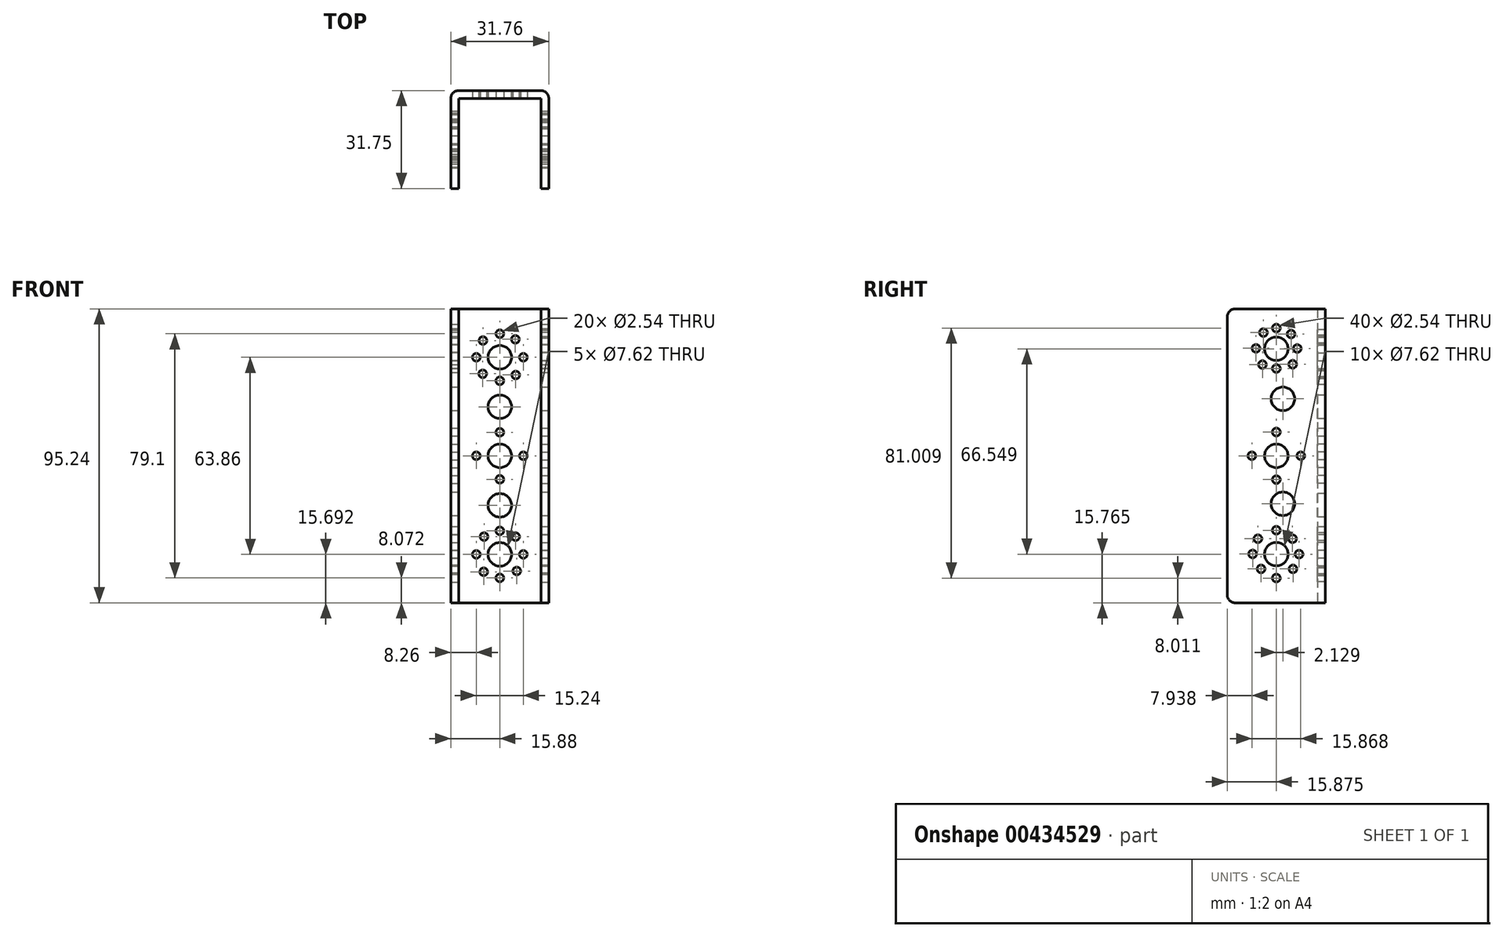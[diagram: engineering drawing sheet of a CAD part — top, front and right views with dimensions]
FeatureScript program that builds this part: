
annotation { "Feature Type Name" : "Feature", "Feature Type Description" : "" }
export const myFeature = defineFeature(function(context is Context, id is Id, definition is map)
    precondition{}
    {
        {
            var Q0;
            Q0=qCreatedBy(makeId("Front.planeOp"),FACE);
            var sketch = newSketch(context, id + "F0", { "sketchPlane" : qUnion([Q0])});
            skLineSegment(sketch, "E0.bottom", {"start": v(-15.87, 47.63) * mm, "end": v(15.88, 47.63) * mm});
            skLineSegment(sketch, "E0.top", {"start": v(-15.88, -47.62) * mm, "end": v(15.88, -47.62) * mm});
            skLineSegment(sketch, "E0.left", {"start": v(-15.87, 47.63) * mm, "end": v(-15.88, -47.62) * mm});
            skLineSegment(sketch, "E0.right", {"start": v(15.88, 47.63) * mm, "end": v(15.88, -47.62) * mm});
            skPoint(sketch, "E0.middle", {"position": v(0, 0) * mm});
            skSolve(sketch);
        }
        {
            var Q0;
            Q0=makeQuery(id+"F0.imprint","IMPRINT",FACE,{"disambiguationData":[TD([[makeQuery(id+"F0.imprint","IMPRINT",EDGE,{"derivedFrom":sQuery(id+"F0.wireOp",EDGE,"E0.bottom")}),-1.0]])]});
            extrude(context, id + "F1", {"entities" : qUnion([Q0]), "flatOperationType" : FlatOperationType.REMOVE, "offsetDistance" : 25.4 * mm, "depth" : 31.75 * mm, "domain" : OperationDomain.MODEL});
        }
        {
            var Q0;
            Q0=makeQuery(id+"F1.opExtrude","CAP_FACE",FACE,{"disambiguationData":[OSD([sQuery(id+"F0.wireOp",EDGE,"E0.bottom"),sQuery(id+"F0.wireOp",EDGE,"E0.top"),sQuery(id+"F0.wireOp",EDGE,"E0.left"),sQuery(id+"F0.wireOp",EDGE,"E0.right")])],"isStart":false});
            var Q1;
            Q1=makeQuery(id+"F1.opExtrude","SWEPT_FACE",FACE,{"disambiguationData":[OSD([sQuery(id+"F0.wireOp",EDGE,"E0.bottom")])]});
            var Q2;
            Q2=makeQuery(id+"F1.opExtrude","SWEPT_FACE",FACE,{"disambiguationData":[OSD([sQuery(id+"F0.wireOp",EDGE,"E0.top")])]});
            shell(context, id + "F2", {"entities" : qUnion([Q0, Q1, Q2]), "thickness" : 2.54 * mm});
        }
        {
            var Q0;
            {var subQ0=sQuery(id+"F0.wireOp",EDGE,"E0.right");var subQ1=sQuery(id+"F0.wireOp",EDGE,"E0.left");var subQ2=sQuery(id+"F0.wireOp",EDGE,"E0.top");var subQ3=sQuery(id+"F0.wireOp",EDGE,"E0.bottom");Q0=makeQuery(id+"F2.opShell","OFFSET_FACE",FACE,{"disambiguationData":[OSD([subQ3,subQ2,subQ1,subQ0]),TDD([makeQuery(id+"F1.opExtrude","CAP_FACE",FACE,{"disambiguationData":[OSD([subQ3,subQ2,subQ1,subQ0])],"isStart":true})])]});}
            var sketch = newSketch(context, id + "F3", { "sketchPlane" : qUnion([Q0])});
            skCircle(sketch, "E1", {"center": v(0, 0) * mm, "radius": 3.81 * mm});
            skPoint(sketch, "E2.centerSnap0", {"position": v(-13.33, 0) * mm});
            skSolve(sketch);
        }
        {
            var Q0;
            Q0=sQuery(id+"F3.wireOp",VERTEX,"E1.center");
            var Q1;
            Q1=makeQuery(id+"F1.opExtrude","SWEPT_BODY",BODY,{"disambiguationData":[OSD([sQuery(id+"F0.wireOp",EDGE,"E0.bottom"),sQuery(id+"F0.wireOp",EDGE,"E0.top"),sQuery(id+"F0.wireOp",EDGE,"E0.left"),sQuery(id+"F0.wireOp",EDGE,"E0.right")])]});
            hole(context, id + "F4", {"style" : HoleStyle.SIMPLE, "endStyle" : HoleEndStyle.THROUGH, "holeDiameter" : 7.62 * mm, "tappedDepth" : 12.7 * mm, "tapClearance" : 3, "locations" : qUnion([Q0]), "scope" : qUnion([Q1])});
        }
        {
            var Q0;
            Q0=makeQuery(id+"F1.opExtrude","CAP_EDGE",EDGE,{"disambiguationData":[OSD([sQuery(id+"F0.wireOp",EDGE,"E0.right")])],"isStart":true});
            var Q1;
            Q1=makeQuery(id+"F1.opExtrude","CAP_EDGE",EDGE,{"disambiguationData":[OSD([sQuery(id+"F0.wireOp",EDGE,"E0.left")])],"isStart":true});
            var Q2;
            Q2=makeQuery(id+"F1.opExtrude","CAP_EDGE",EDGE,{"disambiguationData":[OSD([sQuery(id+"F0.wireOp",EDGE,"E0.bottom")])],"isStart":false});
            var Q3;
            {var subQ0=sQuery(id+"F0.wireOp",EDGE,"E0.bottom");Q3=makeQuery(id+"F2.opShell","OFFSET_EDGE",EDGE,{"disambiguationData":[OSD([subQ0]),TDD([makeQuery(id+"F1.opExtrude","CAP_EDGE",EDGE,{"disambiguationData":[OSD([subQ0])],"isStart":false})])]});}
            var Q4;
            Q4=makeQuery(id+"F1.opExtrude","CAP_EDGE",EDGE,{"disambiguationData":[OSD([sQuery(id+"F0.wireOp",EDGE,"E0.top")])],"isStart":false});
            var Q5;
            {var subQ0=sQuery(id+"F0.wireOp",EDGE,"E0.top");Q5=makeQuery(id+"F2.opShell","OFFSET_EDGE",EDGE,{"disambiguationData":[OSD([subQ0]),TDD([makeQuery(id+"F1.opExtrude","CAP_EDGE",EDGE,{"disambiguationData":[OSD([subQ0])],"isStart":false})])]});}
            fillet(context, id + "F5", {"entities" : qUnion([Q0, Q1, Q2, Q3, Q4, Q5]), "radius" : 2.54 * mm, "tangentPropagation" : true, "allowEdgeOverflow" : false});
        }
        {
            var Q0;
            {var subQ0=sQuery(id+"F0.wireOp",EDGE,"E0.right");var subQ1=sQuery(id+"F0.wireOp",EDGE,"E0.left");var subQ2=sQuery(id+"F0.wireOp",EDGE,"E0.top");var subQ3=sQuery(id+"F0.wireOp",EDGE,"E0.bottom");Q0=makeQuery(id+"F2.opShell","OFFSET_FACE",FACE,{"disambiguationData":[OSD([subQ3,subQ2,subQ1,subQ0]),TDD([makeQuery(id+"F1.opExtrude","CAP_FACE",FACE,{"disambiguationData":[OSD([subQ3,subQ2,subQ1,subQ0])],"isStart":true})])]});}
            var sketch = newSketch(context, id + "F6", { "sketchPlane" : qUnion([Q0])});
            skCircle(sketch, "E3", {"center": v(0, 7.62) * mm, "radius": 1.27 * mm});
            skCircle(sketch, "E4", {"center": v(7.62, 0) * mm, "radius": 1.27 * mm});
            skCircle(sketch, "E5", {"center": v(-7.62, 0) * mm, "radius": 1.27 * mm});
            skCircle(sketch, "E6", {"center": v(0, -7.62) * mm, "radius": 1.27 * mm});
            skSolve(sketch);
        }
        {
            var Q0;
            Q0=sQuery(id+"F6.wireOp",VERTEX,"E3.center");
            var Q1;
            Q1=sQuery(id+"F6.wireOp",VERTEX,"E4.center");
            var Q2;
            Q2=sQuery(id+"F6.wireOp",VERTEX,"E6.center");
            var Q3;
            Q3=sQuery(id+"F6.wireOp",VERTEX,"E5.center");
            var Q4;
            Q4=makeQuery(id+"F1.opExtrude","SWEPT_BODY",BODY,{"disambiguationData":[OSD([sQuery(id+"F0.wireOp",EDGE,"E0.bottom"),sQuery(id+"F0.wireOp",EDGE,"E0.top"),sQuery(id+"F0.wireOp",EDGE,"E0.left"),sQuery(id+"F0.wireOp",EDGE,"E0.right")])]});
            hole(context, id + "F7", {"style" : HoleStyle.SIMPLE, "endStyle" : HoleEndStyle.THROUGH, "holeDiameter" : 2.54 * mm, "tappedDepth" : 12.7 * mm, "tapClearance" : 3, "locations" : qUnion([Q0, Q1, Q2, Q3]), "scope" : qUnion([Q4])});
        }
        {
            var Q0;
            {var subQ0=sQuery(id+"F0.wireOp",EDGE,"E0.right");var subQ1=sQuery(id+"F0.wireOp",EDGE,"E0.left");var subQ2=sQuery(id+"F0.wireOp",EDGE,"E0.top");var subQ3=sQuery(id+"F0.wireOp",EDGE,"E0.bottom");Q0=makeQuery(id+"F2.opShell","OFFSET_FACE",FACE,{"disambiguationData":[OSD([subQ3,subQ2,subQ1,subQ0]),TDD([makeQuery(id+"F1.opExtrude","CAP_FACE",FACE,{"disambiguationData":[OSD([subQ3,subQ2,subQ1,subQ0])],"isStart":true})])]});}
            var sketch = newSketch(context, id + "F8", { "sketchPlane" : qUnion([Q0])});
            skCircle(sketch, "E7", {"center": v(0, 31.93) * mm, "radius": 3.81 * mm});
            skCircle(sketch, "E8", {"center": v(0, -31.93) * mm, "radius": 3.81 * mm});
            skSolve(sketch);
        }
        {
            var Q0;
            Q0=sQuery(id+"F8.wireOp",VERTEX,"E7.center");
            var Q1;
            Q1=sQuery(id+"F8.wireOp",VERTEX,"E8.center");
            var Q2;
            Q2=makeQuery(id+"F1.opExtrude","SWEPT_BODY",BODY,{"disambiguationData":[OSD([sQuery(id+"F0.wireOp",EDGE,"E0.bottom"),sQuery(id+"F0.wireOp",EDGE,"E0.top"),sQuery(id+"F0.wireOp",EDGE,"E0.left"),sQuery(id+"F0.wireOp",EDGE,"E0.right")])]});
            hole(context, id + "F9", {"style" : HoleStyle.SIMPLE, "endStyle" : HoleEndStyle.THROUGH, "holeDiameter" : 7.62 * mm, "tappedDepth" : 12.7 * mm, "tapClearance" : 3, "locations" : qUnion([Q0, Q1]), "scope" : qUnion([Q2])});
        }
        {
            var Q0;
            {var subQ0=sQuery(id+"F0.wireOp",EDGE,"E0.right");var subQ1=sQuery(id+"F0.wireOp",EDGE,"E0.left");var subQ2=sQuery(id+"F0.wireOp",EDGE,"E0.top");var subQ3=sQuery(id+"F0.wireOp",EDGE,"E0.bottom");Q0=makeQuery(id+"F2.opShell","OFFSET_FACE",FACE,{"disambiguationData":[OSD([subQ3,subQ2,subQ1,subQ0]),TDD([makeQuery(id+"F1.opExtrude","CAP_FACE",FACE,{"disambiguationData":[OSD([subQ3,subQ2,subQ1,subQ0])],"isStart":true})])]});}
            var sketch = newSketch(context, id + "F10", { "sketchPlane" : qUnion([Q0])});
            skCircle(sketch, "E9", {"center": v(0, 39.55) * mm, "radius": 1.27 * mm});
            skCircle(sketch, "E10", {"center": v(7.62, 31.93) * mm, "radius": 1.27 * mm});
            skCircle(sketch, "E11", {"center": v(0, 24.31) * mm, "radius": 1.27 * mm});
            skCircle(sketch, "E12", {"center": v(-7.62, 31.93) * mm, "radius": 1.27 * mm});
            skPoint(sketch, "E13.start.orphan", {"position": v(0, 31.93) * mm});
            skCircle(sketch, "E14", {"center": v(-5.47, 37.35) * mm, "radius": 1.27 * mm});
            skCircle(sketch, "E15", {"center": v(5.04, 37.77) * mm, "radius": 1.27 * mm});
            skCircle(sketch, "E16", {"center": v(5.14, 26.2) * mm, "radius": 1.27 * mm});
            skCircle(sketch, "E17", {"center": v(-5.54, 26.6) * mm, "radius": 1.27 * mm});
            skCircle(sketch, "E18", {"center": v(0, -24.3) * mm, "radius": 1.27 * mm});
            skCircle(sketch, "E19", {"center": v(7.62, -31.93) * mm, "radius": 1.27 * mm});
            skCircle(sketch, "E20", {"center": v(0, -39.55) * mm, "radius": 1.27 * mm});
            skCircle(sketch, "E21", {"center": v(-7.62, -31.93) * mm, "radius": 1.27 * mm});
            skPoint(sketch, "E22.orphan", {"position": v(0, -31.93) * mm});
            skCircle(sketch, "E23", {"center": v(5.12, -26.18) * mm, "radius": 1.27 * mm});
            skCircle(sketch, "E24", {"center": v(-5.11, -26.17) * mm, "radius": 1.27 * mm});
            skCircle(sketch, "E25", {"center": v(5.5, -37.31) * mm, "radius": 1.27 * mm});
            skCircle(sketch, "E26", {"center": v(-5.21, -37.6) * mm, "radius": 1.27 * mm});
            skSolve(sketch);
        }
        {
            var Q0;
            Q0=sQuery(id+"F10.wireOp",VERTEX,"E14.center");
            var Q1;
            Q1=sQuery(id+"F10.wireOp",VERTEX,"E9.center");
            var Q2;
            Q2=sQuery(id+"F10.wireOp",VERTEX,"E15.center");
            var Q3;
            Q3=sQuery(id+"F10.wireOp",VERTEX,"E10.center");
            var Q4;
            Q4=sQuery(id+"F10.wireOp",VERTEX,"E16.center");
            var Q5;
            Q5=sQuery(id+"F10.wireOp",VERTEX,"E11.center");
            var Q6;
            Q6=sQuery(id+"F10.wireOp",VERTEX,"E17.center");
            var Q7;
            Q7=sQuery(id+"F10.wireOp",VERTEX,"E12.center");
            var Q8;
            Q8=sQuery(id+"F10.wireOp",VERTEX,"E18.center");
            var Q9;
            Q9=sQuery(id+"F10.wireOp",VERTEX,"E23.center");
            var Q10;
            Q10=sQuery(id+"F10.wireOp",VERTEX,"E19.center");
            var Q11;
            Q11=sQuery(id+"F10.wireOp",VERTEX,"E25.center");
            var Q12;
            Q12=sQuery(id+"F10.wireOp",VERTEX,"E20.center");
            var Q13;
            Q13=sQuery(id+"F10.wireOp",VERTEX,"E21.center");
            var Q14;
            Q14=sQuery(id+"F10.wireOp",VERTEX,"E24.center");
            var Q15;
            Q15=sQuery(id+"F10.wireOp",VERTEX,"E26.center");
            var Q16;
            Q16=makeQuery(id+"F1.opExtrude","SWEPT_BODY",BODY,{"disambiguationData":[OSD([sQuery(id+"F0.wireOp",EDGE,"E0.bottom"),sQuery(id+"F0.wireOp",EDGE,"E0.top"),sQuery(id+"F0.wireOp",EDGE,"E0.left"),sQuery(id+"F0.wireOp",EDGE,"E0.right")])]});
            hole(context, id + "F11", {"style" : HoleStyle.SIMPLE, "endStyle" : HoleEndStyle.THROUGH, "holeDiameter" : 2.54 * mm, "tappedDepth" : 12.7 * mm, "tapClearance" : 3, "locations" : qUnion([Q0, Q1, Q2, Q3, Q4, Q5, Q6, Q7, Q8, Q9, Q10, Q11, Q12, Q13, Q14, Q15]), "scope" : qUnion([Q16])});
        }
        {
            var Q0;
            {var subQ0=sQuery(id+"F0.wireOp",EDGE,"E0.right");var subQ1=sQuery(id+"F0.wireOp",EDGE,"E0.left");var subQ2=sQuery(id+"F0.wireOp",EDGE,"E0.top");var subQ3=sQuery(id+"F0.wireOp",EDGE,"E0.bottom");Q0=makeQuery(id+"F2.opShell","OFFSET_FACE",FACE,{"disambiguationData":[OSD([subQ3,subQ2,subQ1,subQ0]),TDD([makeQuery(id+"F1.opExtrude","CAP_FACE",FACE,{"disambiguationData":[OSD([subQ3,subQ2,subQ1,subQ0])],"isStart":true})])]});}
            var sketch = newSketch(context, id + "F12", { "sketchPlane" : qUnion([Q0])});
            skCircle(sketch, "E27", {"center": v(0, -16.04) * mm, "radius": 3.81 * mm});
            skCircle(sketch, "E28", {"center": v(0, 15.9) * mm, "radius": 3.81 * mm});
            skSolve(sketch);
        }
        {
            var Q0;
            Q0=sQuery(id+"F12.wireOp",VERTEX,"E28.center");
            var Q1;
            Q1=sQuery(id+"F12.wireOp",VERTEX,"E27.center");
            var Q2;
            Q2=makeQuery(id+"F1.opExtrude","SWEPT_BODY",BODY,{"disambiguationData":[OSD([sQuery(id+"F0.wireOp",EDGE,"E0.bottom"),sQuery(id+"F0.wireOp",EDGE,"E0.top"),sQuery(id+"F0.wireOp",EDGE,"E0.left"),sQuery(id+"F0.wireOp",EDGE,"E0.right")])]});
            hole(context, id + "F13", {"style" : HoleStyle.SIMPLE, "endStyle" : HoleEndStyle.THROUGH, "holeDiameter" : 7.62 * mm, "tappedDepth" : 12.7 * mm, "tapClearance" : 3, "locations" : qUnion([Q0, Q1]), "scope" : qUnion([Q2])});
        }
        {
            var Q0;
            Q0=makeQuery(id+"F1.opExtrude","SWEPT_FACE",FACE,{"disambiguationData":[OSD([sQuery(id+"F0.wireOp",EDGE,"E0.right")])]});
            var sketch = newSketch(context, id + "F14", { "sketchPlane" : qUnion([Q0])});
            skCircle(sketch, "E29", {"center": v(-15.88, 0) * mm, "radius": 3.81 * mm});
            skCircle(sketch, "E30", {"center": v(-15.88, 34.7) * mm, "radius": 3.81 * mm});
            skCircle(sketch, "E31", {"center": v(-15.88, -31.85) * mm, "radius": 3.81 * mm});
            skPoint(sketch, "E32.centerSnap0", {"position": v(-31.75, 0) * mm});
            skSolve(sketch);
        }
        {
            var Q0;
            Q0=sQuery(id+"F14.wireOp",VERTEX,"E29.center");
            var Q1;
            Q1=sQuery(id+"F14.wireOp",VERTEX,"E30.center");
            var Q2;
            Q2=sQuery(id+"F14.wireOp",VERTEX,"E31.center");
            var Q3;
            Q3=makeQuery(id+"F1.opExtrude","SWEPT_BODY",BODY,{"disambiguationData":[OSD([sQuery(id+"F0.wireOp",EDGE,"E0.bottom"),sQuery(id+"F0.wireOp",EDGE,"E0.top"),sQuery(id+"F0.wireOp",EDGE,"E0.left"),sQuery(id+"F0.wireOp",EDGE,"E0.right")])]});
            hole(context, id + "F15", {"style" : HoleStyle.SIMPLE, "endStyle" : HoleEndStyle.THROUGH, "holeDiameter" : 7.62 * mm, "tappedDepth" : 12.7 * mm, "tapClearance" : 3, "locations" : qUnion([Q0, Q1, Q2]), "scope" : qUnion([Q3])});
        }
        {
            var Q0;
            Q0=makeQuery(id+"F1.opExtrude","SWEPT_FACE",FACE,{"disambiguationData":[OSD([sQuery(id+"F0.wireOp",EDGE,"E0.right")])]});
            var sketch = newSketch(context, id + "F16", { "sketchPlane" : qUnion([Q0])});
            skCircle(sketch, "E33", {"center": v(-7.94, 0) * mm, "radius": 1.27 * mm});
            skCircle(sketch, "E34", {"center": v(-15.87, 7.7) * mm, "radius": 1.27 * mm});
            skCircle(sketch, "E35", {"center": v(-23.81, 0) * mm, "radius": 1.27 * mm});
            skCircle(sketch, "E36", {"center": v(-15.87, -7.7) * mm, "radius": 1.27 * mm});
            skPoint(sketch, "E37.orphan", {"position": v(-13.92, 0) * mm});
            skLineSegment(sketch, "E38", {"start": v(-15.88, 47.63) * mm, "end": v(-15.88, -47.62) * mm});
            skLineSegment(sketch, "E39", {"start": v(-15.87, 7.7) * mm, "end": v(-31.75, 7.7) * mm});
            skLineSegment(sketch, "E40", {"start": v(-31.75, 7.7) * mm, "end": v(-15.87, -7.7) * mm});
            skLineSegment(sketch, "E41", {"start": v(-15.87, -7.7) * mm, "end": v(-31.75, -7.7) * mm});
            skLineSegment(sketch, "E42", {"start": v(-31.75, -7.7) * mm, "end": v(-31.75, 7.7) * mm});
            skSolve(sketch);
        }
        {
            var Q0;
            Q0=sQuery(id+"F16.wireOp",VERTEX,"E34.center");
            var Q1;
            Q1=sQuery(id+"F16.wireOp",VERTEX,"E36.center");
            var Q2;
            Q2=sQuery(id+"F16.wireOp",VERTEX,"E35.center");
            var Q3;
            Q3=sQuery(id+"F16.wireOp",VERTEX,"E33.center");
            var Q4;
            Q4=makeQuery(id+"F1.opExtrude","SWEPT_BODY",BODY,{"disambiguationData":[OSD([sQuery(id+"F0.wireOp",EDGE,"E0.bottom"),sQuery(id+"F0.wireOp",EDGE,"E0.top"),sQuery(id+"F0.wireOp",EDGE,"E0.left"),sQuery(id+"F0.wireOp",EDGE,"E0.right")])]});
            hole(context, id + "F17", {"style" : HoleStyle.SIMPLE, "endStyle" : HoleEndStyle.THROUGH, "holeDiameter" : 2.54 * mm, "tappedDepth" : 12.7 * mm, "tapClearance" : 3, "locations" : qUnion([Q0, Q1, Q2, Q3]), "scope" : qUnion([Q4])});
        }
        {
            var Q0;
            Q0=makeQuery(id+"F1.opExtrude","SWEPT_FACE",FACE,{"disambiguationData":[OSD([sQuery(id+"F0.wireOp",EDGE,"E0.right")])]});
            var sketch = newSketch(context, id + "F18", { "sketchPlane" : qUnion([Q0])});
            skCircle(sketch, "E43", {"center": v(-15.88, 28.3) * mm, "radius": 0.94 * mm});
            skCircle(sketch, "E44", {"center": v(-22.47, 34.83) * mm, "radius": 0.94 * mm});
            skCircle(sketch, "E45", {"center": v(-15.88, 41.4) * mm, "radius": 0.94 * mm});
            skCircle(sketch, "E46", {"center": v(-9.1, 34.78) * mm, "radius": 0.94 * mm});
            skPoint(sketch, "E47.orphan", {"position": v(-15.88, 34.7) * mm});
            skCircle(sketch, "E48", {"center": v(-20.05, 39.94) * mm, "radius": 0.94 * mm});
            skCircle(sketch, "E49", {"center": v(-11.1, 39.47) * mm, "radius": 0.94 * mm});
            skCircle(sketch, "E50", {"center": v(-10.57, 29.67) * mm, "radius": 0.94 * mm});
            skCircle(sketch, "E51", {"center": v(-20.36, 29.57) * mm, "radius": 0.94 * mm});
            skCircle(sketch, "E52", {"center": v(-15.88, -24.11) * mm, "radius": 1.27 * mm});
            skCircle(sketch, "E53", {"center": v(-8.51, -31.86) * mm, "radius": 1.27 * mm});
            skCircle(sketch, "E54", {"center": v(-15.88, -39.6) * mm, "radius": 1.27 * mm});
            skCircle(sketch, "E55", {"center": v(-23.55, -31.8) * mm, "radius": 1.27 * mm});
            skCircle(sketch, "E56", {"center": v(-10.61, -26.87) * mm, "radius": 1.27 * mm});
            skCircle(sketch, "E57", {"center": v(-21.85, -26.87) * mm, "radius": 1.27 * mm});
            skCircle(sketch, "E58", {"center": v(-20.83, -36.65) * mm, "radius": 1.27 * mm});
            skCircle(sketch, "E59", {"center": v(-10.48, -36.65) * mm, "radius": 1.27 * mm});
            skPoint(sketch, "E60.orphan", {"position": v(-15.88, -31.85) * mm});
            skPoint(sketch, "E61.orphan", {"position": v(-15.88, 47.63) * mm});
            skLineSegment(sketch, "E62", {"start": v(-15.88, 47.63) * mm, "end": v(-15.88, -47.62) * mm});
            skLineSegment(sketch, "E63", {"start": v(-15.88, -24.11) * mm, "end": v(-31.75, -24.11) * mm});
            skLineSegment(sketch, "E64", {"start": v(-31.75, -24.11) * mm, "end": v(-23.55, -31.8) * mm});
            skLineSegment(sketch, "E65", {"start": v(-15.88, -39.6) * mm, "end": v(-31.75, -39.6) * mm});
            skLineSegment(sketch, "E66", {"start": v(-31.75, -39.6) * mm, "end": v(-23.55, -31.8) * mm});
            skLineSegment(sketch, "E67", {"start": v(-23.55, -31.8) * mm, "end": v(-8.51, -31.8) * mm});
            skLineSegment(sketch, "E68", {"start": v(-20.83, -36.65) * mm, "end": v(-10.48, -36.65) * mm});
            skLineSegment(sketch, "E69", {"start": v(-10.48, -36.65) * mm, "end": v(-21.85, -26.87) * mm});
            skLineSegment(sketch, "E70", {"start": v(-20.83, -36.65) * mm, "end": v(-10.61, -26.87) * mm});
            skLineSegment(sketch, "E71", {"start": v(-10.61, -26.87) * mm, "end": v(-21.85, -26.87) * mm});
            skSolve(sketch);
        }
        {
            var Q0;
            Q0=sQuery(id+"F18.wireOp",VERTEX,"E48.center");
            var Q1;
            Q1=sQuery(id+"F18.wireOp",VERTEX,"E45.center");
            var Q2;
            Q2=sQuery(id+"F18.wireOp",VERTEX,"E49.center");
            var Q3;
            Q3=sQuery(id+"F18.wireOp",VERTEX,"E46.center");
            var Q4;
            Q4=sQuery(id+"F18.wireOp",VERTEX,"E50.center");
            var Q5;
            Q5=sQuery(id+"F18.wireOp",VERTEX,"E43.center");
            var Q6;
            Q6=sQuery(id+"F18.wireOp",VERTEX,"E51.center");
            var Q7;
            Q7=sQuery(id+"F18.wireOp",VERTEX,"E44.center");
            var Q8;
            Q8=sQuery(id+"F18.wireOp",VERTEX,"E52.center");
            var Q9;
            Q9=sQuery(id+"F18.wireOp",VERTEX,"E56.center");
            var Q10;
            Q10=sQuery(id+"F18.wireOp",VERTEX,"E53.center");
            var Q11;
            Q11=sQuery(id+"F18.wireOp",VERTEX,"E59.center");
            var Q12;
            Q12=sQuery(id+"F18.wireOp",VERTEX,"E54.center");
            var Q13;
            Q13=sQuery(id+"F18.wireOp",VERTEX,"E58.center");
            var Q14;
            Q14=sQuery(id+"F18.wireOp",VERTEX,"E55.center");
            var Q15;
            Q15=sQuery(id+"F18.wireOp",VERTEX,"E57.center");
            var Q16;
            Q16=makeQuery(id+"F1.opExtrude","SWEPT_BODY",BODY,{"disambiguationData":[OSD([sQuery(id+"F0.wireOp",EDGE,"E0.bottom"),sQuery(id+"F0.wireOp",EDGE,"E0.top"),sQuery(id+"F0.wireOp",EDGE,"E0.left"),sQuery(id+"F0.wireOp",EDGE,"E0.right")])]});
            hole(context, id + "F19", {"style" : HoleStyle.SIMPLE, "endStyle" : HoleEndStyle.THROUGH, "holeDiameter" : 2.54 * mm, "majorDiameter" : 6.35 * mm, "tappedDepth" : 12.7 * mm, "tapClearance" : 3, "locations" : qUnion([Q0, Q1, Q2, Q3, Q4, Q5, Q6, Q7, Q8, Q9, Q10, Q11, Q12, Q13, Q14, Q15]), "scope" : qUnion([Q16])});
        }
        {
            var Q0;
            Q0=makeQuery(id+"F1.opExtrude","SWEPT_FACE",FACE,{"disambiguationData":[OSD([sQuery(id+"F0.wireOp",EDGE,"E0.right")])]});
            var sketch = newSketch(context, id + "F20", { "sketchPlane" : qUnion([Q0])});
            skCircle(sketch, "E72", {"center": v(-13.75, -15.53) * mm, "radius": 3.81 * mm});
            skCircle(sketch, "E73", {"center": v(-13.75, 18.47) * mm, "radius": 3.81 * mm});
            skSolve(sketch);
        }
        {
            var Q0;
            Q0=sQuery(id+"F20.wireOp",VERTEX,"E73.center");
            var Q1;
            Q1=sQuery(id+"F20.wireOp",VERTEX,"E72.center");
            var Q2;
            Q2=makeQuery(id+"F1.opExtrude","SWEPT_BODY",BODY,{"disambiguationData":[OSD([sQuery(id+"F0.wireOp",EDGE,"E0.bottom"),sQuery(id+"F0.wireOp",EDGE,"E0.top"),sQuery(id+"F0.wireOp",EDGE,"E0.left"),sQuery(id+"F0.wireOp",EDGE,"E0.right")])]});
            hole(context, id + "F21", {"style" : HoleStyle.SIMPLE, "endStyle" : HoleEndStyle.THROUGH, "holeDiameter" : 7.62 * mm, "tappedDepth" : 12.7 * mm, "tapClearance" : 3, "locations" : qUnion([Q0, Q1]), "scope" : qUnion([Q2])});
        }
    });
